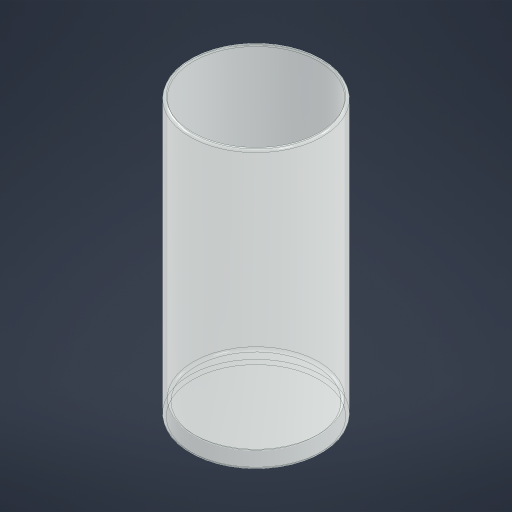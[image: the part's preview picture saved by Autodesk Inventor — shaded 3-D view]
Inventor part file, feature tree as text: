
AUTODESK INVENTOR PART (.ipt)
format: ipt  version: 2024.3 (Build 283343000, 343)  size: 204,288 bytes
history: native  units: mm
features: fillet x3, extrude x2, sketch x2
ambient origin geometry x8: Origin, YZ Plane, XZ Plane, XY Plane, X Axis, Y Axis, Z Axis, Center Point
bodies: Body1 (feature_tree)
feature tree (7):
  extrude  "Extrusion2"  Depth=10.0mm TaperAngle=0.0deg
  extrude  "Extrusion3"  Depth=2.0mm
  fillet  "Fillet1"  Radius=200.0mm
  fillet  "Fillet2"  Radius=2.0mm
  fillet  "Fillet3"  Radius=2.0mm
  sketch  "Sketch2"  dims[d4=100.0mm d5=10.0mm d6=0.0mm]
  sketch  "Sketch3"  dims[d7=100.0mm d8=95.0mm d9=200.0mm d10=0.0mm d11=2.0mm d12=2.0mm d13=2.0mm]
